# Revit family: 2093164 Sylvania Lighting Fixture MC2 TRIM 0-9M 4K DALI WHT OPAL
name_source: partatom
category: Lighting Fixtures
revit_build: Autodesk Revit 2016 (Build: 20150220_1215(x64)
units: mm (PartAtom-declared; Revit-internal decimal feet)

## family parameters
Cut with Voids When Loaded = No
Host = Face
Light Source = Yes
OmniClass Number = 23.80.70.11.17
OmniClass Title = Specialized Lighting by Location or Use
Part Type = Normal
Room Calculation Point = No
Round Connector Dimension = Use Diameter
Shared = No

## types (1)
- 2093164 MC2 TRIM 0.9M 4K DALI WHT OPAL
    Apparent Load = 16 VA
    Assembly Code = D5020200
    AssetType = Fixed
    Color Filter = 16777215
    Default Elevation = 0 mm  [stored 0 ft]
    Description = Mini Continuum II introduces a uniquely clean, simple LED lighting system offering continuous, highly uniform lines of light across walls and ceilings. This highly versatile lighting tool can be recessed, semi-recessed, surface-mounted or suspended, either vertically or horizontally. Available as direct/indirect or direct only distribution - both of which can be interconnected. Every batten has a plug and socket arrangement for easy and rapid electrical installation. Mini Continuum II Direct is available in two versions: one with an outside trim detail for plasterboard ceilings; and a trimless version for when a seamless effect is required. Dimmable DALI versions and 3hr non-maintained integral emergency options are available as standard options
    Dimming Lamp Color Temperature Shift = <None>
    DocumentationLiterature = http://www.sylvania-lighting.com
    DurationUnit = hours
    ElectricShockClassification = Class I
    Emit Shape Visible in Rendering = No
    Emit from Rectangle Length = 900 mm  [stored 2.95276 ft]
    Emit from Rectangle Width = 52 mm  [stored 0.170604 ft]
    ExpectedLife = 50000
    Height_SYL = 86 mm
    IfcExportAs = IfcLightFixtureType
    IfcExportType = IfcLightFixtureType
    IngressProtection = IP20
    Keynote = 16500
    Lamp = LED
    LampColourRenderingIndex = 80
    LampColourTemperature = 4000 K
    LampMacAdamStep = 3
    LampNominalLuminous = 1787 lm
    LampsType = LED
    Length_SYL = 900 mm  [stored 2.95276 ft]
    LightOutputRatio = 100
    LuminousEfficacy = 112 lm/W
    Manufacturer = Feilo Sylvania
    ManufacturerName = Feilo Sylvania
    Material = aluminium housing, polycarbonate diffuser
    Material_1_SYL = Metal_Sylvania_Mini Continuum II_White
    Material_2_SYL = Polycarbonate_Sylvania_Mini Continuum II_Opal_4000K
    Material_3_SYL = Metal_Sylvania_Mini Contiuum II_Silver
    Model = MC2 TRIM 0.9M 4K DALI WHT OPAL
    ModelNumber = 2093164
    ModelReference = MC2 TRIM 0.9M 4K DALI WHT OPAL
    Name = MC2 TRIM 0.9M 4K DALI WHT OPAL
    NominalHeight = 86 mm
    NominalLength = 900 mm  [stored 2.95276 ft]
    NominalWidth = 0 mm  [stored 0 ft]
    Photometric Web File = 2093164.ies
    PowerConsumption = 16 W
    PowerFactor = 0.95
    Tilt Angle = -90.00°
    TypeName = MC2 TRIM 0.9M 4K DALI WHT OPAL
    URL = http://www.sylvania-lighting.com
    Voltage = 0 V
    Weight = 1.8 kg
    Width_SYL = 54 mm

note: [stored X ft] marks values corroborated as IEEE doubles in the binary element streams (Revit-internal decimal feet)

## geometry (parser evidence)
native form markers: Sweep x2
no freeform markers — native parametric forms only
